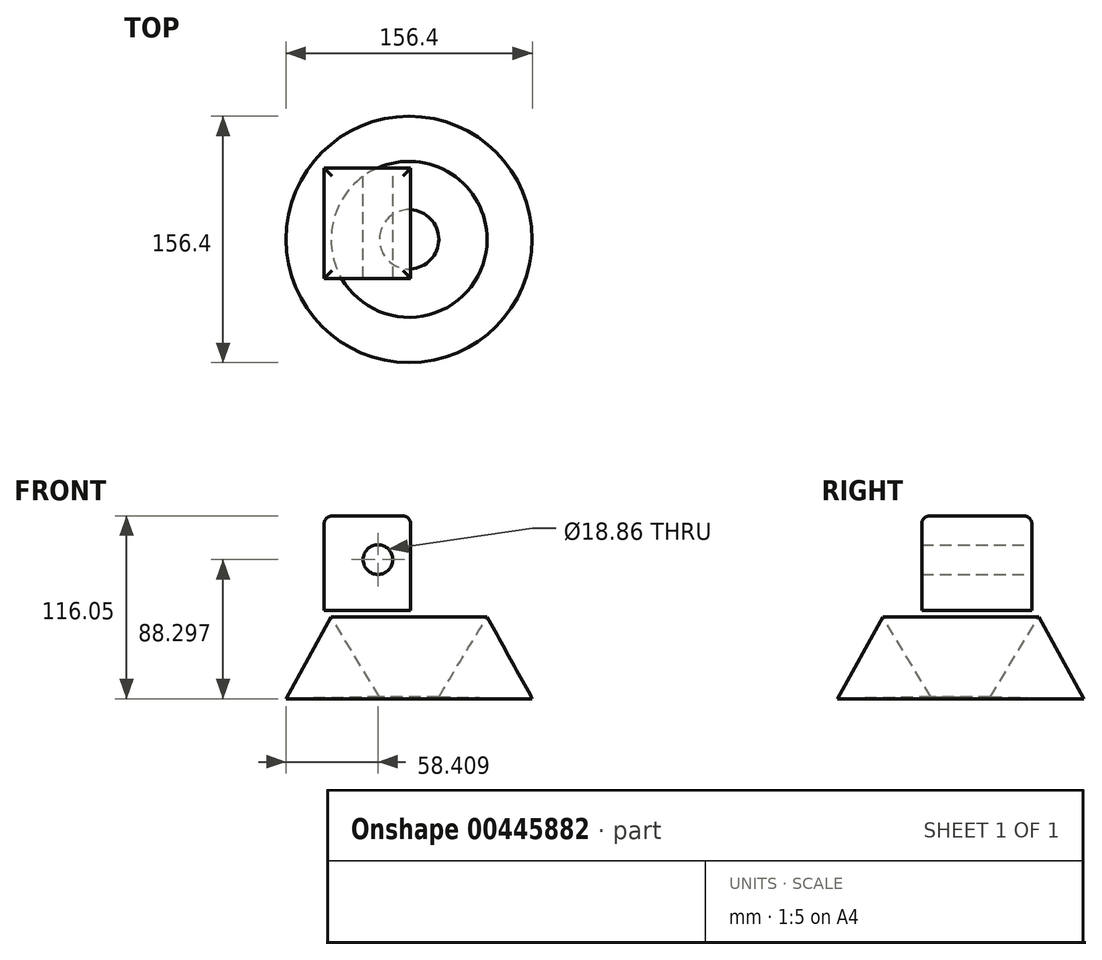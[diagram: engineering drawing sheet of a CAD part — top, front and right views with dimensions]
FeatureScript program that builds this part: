
annotation { "Feature Type Name" : "Feature", "Feature Type Description" : "" }
export const myFeature = defineFeature(function(context is Context, id is Id, definition is map)
    precondition{}
    {
        {
            var Q0;
            Q0=qCreatedBy(makeId("Top.planeOp"),FACE);
            var sketch = newSketch(context, id + "F0", { "sketchPlane" : qUnion([Q0])});
            skLineSegment(sketch, "E0.bottom", {"start": v(-54, -24.74) * mm, "end": v(1, -24.74) * mm});
            skLineSegment(sketch, "E0.top", {"start": v(-54, 45.26) * mm, "end": v(1, 45.26) * mm});
            skLineSegment(sketch, "E0.left", {"start": v(-54, -24.74) * mm, "end": v(-54, 45.26) * mm});
            skLineSegment(sketch, "E0.right", {"start": v(1, -24.74) * mm, "end": v(1, 45.26) * mm});
            skSolve(sketch);
        }
        {
            var Q0;
            Q0=makeQuery(id+"F0.imprint","IMPRINT",FACE,{"disambiguationData":[TD([[makeQuery(id+"F0.imprint","IMPRINT",EDGE,{"derivedFrom":sQuery(id+"F0.wireOp",EDGE,"E0.bottom")}),1.0]])]});
            extrude(context, id + "F1", {"entities" : qUnion([Q0]), "depth" : 60 * mm});
        }
        {
            var Q0;
            Q0=makeQuery(id+"F1.opExtrude","SWEPT_FACE",FACE,{"disambiguationData":[OSD([sQuery(id+"F0.wireOp",EDGE,"E0.top")])]});
            var sketch = newSketch(context, id + "F2", { "sketchPlane" : qUnion([Q0])});
            skCircle(sketch, "E1", {"center": v(19.8, 32.25) * mm, "radius": 9.43 * mm});
            skSolve(sketch);
        }
        {
            var Q0;
            Q0=makeQuery(id+"F2.imprint","IMPRINT",FACE,{"disambiguationData":[TD([[makeQuery(id+"F2.imprint","IMPRINT",EDGE,{"derivedFrom":sQuery(id+"F2.wireOp",EDGE,"E1")}),1.0]])]});
            extrude(context, id + "F3", {"entities" : qUnion([Q0]), "operationType" : NewBodyOperationType.REMOVE, "oppositeDirection" : true, "depth" : 90 * mm});
        }
        {
            var Q0;
            Q0=makeQuery(id+"F1.opExtrude","CAP_FACE",FACE,{"disambiguationData":[OSD([sQuery(id+"F0.wireOp",EDGE,"E0.bottom"),sQuery(id+"F0.wireOp",EDGE,"E0.top"),sQuery(id+"F0.wireOp",EDGE,"E0.left"),sQuery(id+"F0.wireOp",EDGE,"E0.right")])],"isStart":false});
            fillet(context, id + "F4", {"entities" : qUnion([Q0]), "radius" : 5 * mm, "tangentPropagation" : true, "allowEdgeOverflow" : false});
        }
        {
            var Q0;
            Q0=qCreatedBy(makeId("Front.planeOp"),FACE);
            var sketch = newSketch(context, id + "F5", { "sketchPlane" : qUnion([Q0])});
            skLineSegment(sketch, "E2", {"start": v(0, 0) * mm, "end": v(0, -73.21) * mm});
            skCircle(sketch, "E3.cCircle", {"center": v(-48.86, -38.34) * mm, "radius": 17.14 * mm, "construction": true});
            skLineSegment(sketch, "E3.0", {"start": v(-49.53, -4.07) * mm, "end": v(-18.84, -54.89) * mm});
            skLineSegment(sketch, "E3.1", {"start": v(-18.84, -54.89) * mm, "end": v(-78.2, -56.05) * mm});
            skLineSegment(sketch, "E3.2", {"start": v(-78.2, -56.05) * mm, "end": v(-49.53, -4.07) * mm});
            skPoint(sketch, "E3.0.midPoint", {"position": v(-34.18, -29.48) * mm});
            skSolve(sketch);
        }
        {
            var Q0;
            Q0=makeQuery(id+"F5.imprint","IMPRINT",FACE,{"disambiguationData":[TD([[makeQuery(id+"F5.imprint","IMPRINT",EDGE,{"derivedFrom":sQuery(id+"F5.wireOp",EDGE,"E3.0")}),-1.0]])]});
            var Q1;
            Q1=sQuery(id+"F5.wireOp",EDGE,"E2");
            revolve(context, id + "F6", {"entities" : qUnion([Q0]), "axis" : qUnion([Q1]), "revolveType" : RevolveType.FULL});
        }
    });
